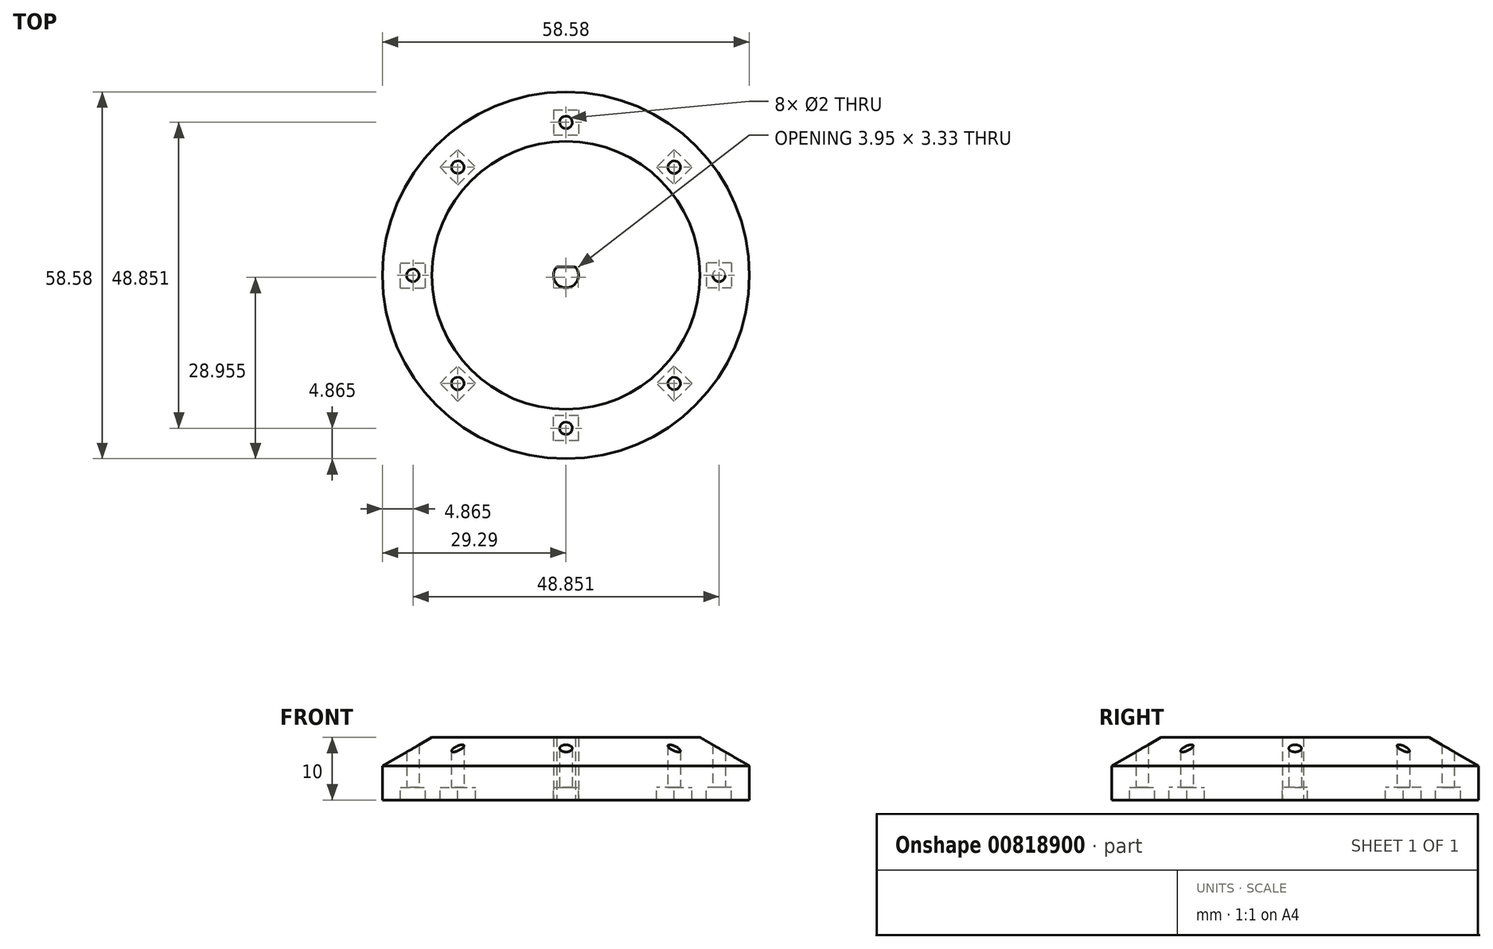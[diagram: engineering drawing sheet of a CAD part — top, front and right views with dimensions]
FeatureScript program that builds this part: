
annotation { "Feature Type Name" : "Feature", "Feature Type Description" : "" }
export const myFeature = defineFeature(function(context is Context, id is Id, definition is map)
    precondition{}
    {
        {
            var Q0;
            Q0=qCreatedBy(makeId("Top.planeOp"),FACE);
            var sketch = newSketch(context, id + "F0", { "sketchPlane" : qUnion([Q0])});
            skCircle(sketch, "E0", {"center": v(0, 0) * mm, "radius": 29.29 * mm});
            skCircle(sketch, "E1", {"center": v(0, 24.43) * mm, "radius": 1 * mm});
            skCircle(sketch, "E2.1.0", {"center": v(-17.27, 17.27) * mm, "radius": 1 * mm});
            skCircle(sketch, "E2.2.0", {"center": v(-24.43, 0) * mm, "radius": 1 * mm});
            skCircle(sketch, "E2.3.0", {"center": v(-17.27, -17.27) * mm, "radius": 1 * mm});
            skCircle(sketch, "E2.4.0", {"center": v(0, -24.43) * mm, "radius": 1 * mm});
            skCircle(sketch, "E2.5.0", {"center": v(17.27, -17.27) * mm, "radius": 1 * mm});
            skCircle(sketch, "E2.6.0", {"center": v(24.43, 0) * mm, "radius": 1 * mm});
            skCircle(sketch, "E2.7.0", {"center": v(17.27, 17.27) * mm, "radius": 1 * mm});
            skArc(sketch, "E3", {"start": v(-1.5, 1.33) * mm, "mid": v(0, -2) * mm, "end": v(1.5, 1.33) * mm});
            skLineSegment(sketch, "E4", {"start": v(-1.5, 1.33) * mm, "end": v(1.5, 1.33) * mm});
            skSolve(sketch);
        }
        {
            var Q0;
            Q0=makeQuery(id+"F0.imprint","IMPRINT",FACE,{"disambiguationData":[TD([[makeQuery(id+"F0.imprint","IMPRINT",EDGE,{"derivedFrom":sQuery(id+"F0.wireOp",EDGE,"E0")}),1.0]])]});
            extrude(context, id + "F1", {"entities" : qUnion([Q0]), "depth" : 10 * mm, "offsetDistance" : 25 * mm});
        }
        {
            var Q0;
            Q0=makeQuery(id+"F1.opExtrude","CAP_EDGE",EDGE,{"disambiguationData":[OSD([sQuery(id+"F0.wireOp",EDGE,"E0")])],"isStart":false});
            chamfer(context, id + "F2", {"entities" : qUnion([Q0]), "chamferType" : ChamferType.TWO_OFFSETS, "width1" : 7.9 * mm, "oppositeDirection" : false, "width2" : 4.56 * mm, "tangentPropagation" : true});
        }
        {
            var Q0;
            Q0=qCreatedBy(makeId("Top.planeOp"),FACE);
            cPlane(context, id + "F3", {"entities" : qUnion([Q0]), "cplaneType" : CPlaneType.OFFSET, "offset" : 2 * mm, "width" : 150 * mm, "height" : 150 * mm});
        }
        {
            var Q0;
            Q0=qCreatedBy(id+"F3.planeOp",FACE);
            var sketch = newSketch(context, id + "F4", { "sketchPlane" : qUnion([Q0])});
            skCircle(sketch, "E5.0", {"center": v(0, -24.43) * mm, "radius": 1 * mm});
            skLineSegment(sketch, "E6.bottom", {"start": v(2, -26.43) * mm, "end": v(-2, -26.43) * mm});
            skLineSegment(sketch, "E6.top", {"start": v(2, -22.43) * mm, "end": v(-2, -22.43) * mm});
            skLineSegment(sketch, "E6.left", {"start": v(2, -26.43) * mm, "end": v(2, -22.43) * mm});
            skLineSegment(sketch, "E6.right", {"start": v(-2, -26.43) * mm, "end": v(-2, -22.43) * mm});
            skLineSegment(sketch, "E7.1.0", {"start": v(20.1, -17.27) * mm, "end": v(17.27, -20.1) * mm});
            skLineSegment(sketch, "E7.1.1", {"start": v(17.27, -20.1) * mm, "end": v(14.44, -17.27) * mm});
            skLineSegment(sketch, "E7.1.2", {"start": v(17.27, -14.44) * mm, "end": v(14.44, -17.27) * mm});
            skLineSegment(sketch, "E7.1.3", {"start": v(20.1, -17.27) * mm, "end": v(17.27, -14.44) * mm});
            skLineSegment(sketch, "E7.2.0", {"start": v(26.43, 2) * mm, "end": v(26.43, -2) * mm});
            skLineSegment(sketch, "E7.2.1", {"start": v(26.43, -2) * mm, "end": v(22.43, -2) * mm});
            skLineSegment(sketch, "E7.2.2", {"start": v(22.43, 2) * mm, "end": v(22.43, -2) * mm});
            skLineSegment(sketch, "E7.2.3", {"start": v(26.43, 2) * mm, "end": v(22.43, 2) * mm});
            skLineSegment(sketch, "E7.3.0", {"start": v(17.27, 20.1) * mm, "end": v(20.1, 17.27) * mm});
            skLineSegment(sketch, "E7.3.1", {"start": v(20.1, 17.27) * mm, "end": v(17.27, 14.44) * mm});
            skLineSegment(sketch, "E7.3.2", {"start": v(14.44, 17.27) * mm, "end": v(17.27, 14.44) * mm});
            skLineSegment(sketch, "E7.3.3", {"start": v(17.27, 20.1) * mm, "end": v(14.44, 17.27) * mm});
            skLineSegment(sketch, "E7.4.0", {"start": v(-2, 26.43) * mm, "end": v(2, 26.43) * mm});
            skLineSegment(sketch, "E7.4.1", {"start": v(2, 26.43) * mm, "end": v(2, 22.43) * mm});
            skLineSegment(sketch, "E7.4.2", {"start": v(-2, 22.43) * mm, "end": v(2, 22.43) * mm});
            skLineSegment(sketch, "E7.4.3", {"start": v(-2, 26.43) * mm, "end": v(-2, 22.43) * mm});
            skLineSegment(sketch, "E7.5.0", {"start": v(-20.1, 17.27) * mm, "end": v(-17.27, 20.1) * mm});
            skLineSegment(sketch, "E7.5.1", {"start": v(-17.27, 20.1) * mm, "end": v(-14.44, 17.27) * mm});
            skLineSegment(sketch, "E7.5.2", {"start": v(-17.27, 14.44) * mm, "end": v(-14.44, 17.27) * mm});
            skLineSegment(sketch, "E7.5.3", {"start": v(-20.1, 17.27) * mm, "end": v(-17.27, 14.44) * mm});
            skLineSegment(sketch, "E7.6.0", {"start": v(-26.43, -2) * mm, "end": v(-26.43, 2) * mm});
            skLineSegment(sketch, "E7.6.1", {"start": v(-26.43, 2) * mm, "end": v(-22.43, 2) * mm});
            skLineSegment(sketch, "E7.6.2", {"start": v(-22.43, -2) * mm, "end": v(-22.43, 2) * mm});
            skLineSegment(sketch, "E7.6.3", {"start": v(-26.43, -2) * mm, "end": v(-22.43, -2) * mm});
            skLineSegment(sketch, "E7.7.0", {"start": v(-17.27, -20.1) * mm, "end": v(-20.1, -17.27) * mm});
            skLineSegment(sketch, "E7.7.1", {"start": v(-20.1, -17.27) * mm, "end": v(-17.27, -14.44) * mm});
            skLineSegment(sketch, "E7.7.2", {"start": v(-14.44, -17.27) * mm, "end": v(-17.27, -14.44) * mm});
            skLineSegment(sketch, "E7.7.3", {"start": v(-17.27, -20.1) * mm, "end": v(-14.44, -17.27) * mm});
            skPoint(sketch, "E7.center", {"position": v(0, 0) * mm});
            skSolve(sketch);
        }
        {
            var Q0;
            Q0=makeQuery(id+"F4.imprint","IMPRINT",FACE,{"disambiguationData":[TD([[makeQuery(id+"F4.imprint","IMPRINT",EDGE,{"derivedFrom":sQuery(id+"F4.wireOp",EDGE,"E5.0")}),1.0]])]});
            var Q1;
            Q1=makeQuery(id+"F4.imprint","IMPRINT",FACE,{"disambiguationData":[TD([[makeQuery(id+"F4.imprint","IMPRINT",EDGE,{"derivedFrom":sQuery(id+"F4.wireOp",EDGE,"E5.0")}),-1.0]])]});
            var Q2;
            Q2=makeQuery(id+"F4.imprint","IMPRINT",FACE,{"disambiguationData":[TD([[makeQuery(id+"F4.imprint","IMPRINT",EDGE,{"derivedFrom":sQuery(id+"F4.wireOp",EDGE,"E7.7.0")}),-1.0]])]});
            var Q3;
            Q3=makeQuery(id+"F4.imprint","IMPRINT",FACE,{"disambiguationData":[TD([[makeQuery(id+"F4.imprint","IMPRINT",EDGE,{"derivedFrom":sQuery(id+"F4.wireOp",EDGE,"E7.1.0")}),-1.0]])]});
            var Q4;
            Q4=makeQuery(id+"F4.imprint","IMPRINT",FACE,{"disambiguationData":[TD([[makeQuery(id+"F4.imprint","IMPRINT",EDGE,{"derivedFrom":sQuery(id+"F4.wireOp",EDGE,"E7.6.0")}),-1.0]])]});
            var Q5;
            Q5=makeQuery(id+"F4.imprint","IMPRINT",FACE,{"disambiguationData":[TD([[makeQuery(id+"F4.imprint","IMPRINT",EDGE,{"derivedFrom":sQuery(id+"F4.wireOp",EDGE,"E7.2.0")}),-1.0]])]});
            var Q6;
            Q6=makeQuery(id+"F4.imprint","IMPRINT",FACE,{"disambiguationData":[TD([[makeQuery(id+"F4.imprint","IMPRINT",EDGE,{"derivedFrom":sQuery(id+"F4.wireOp",EDGE,"E7.5.0")}),-1.0]])]});
            var Q7;
            Q7=makeQuery(id+"F4.imprint","IMPRINT",FACE,{"disambiguationData":[TD([[makeQuery(id+"F4.imprint","IMPRINT",EDGE,{"derivedFrom":sQuery(id+"F4.wireOp",EDGE,"E7.3.0")}),-1.0]])]});
            var Q8;
            Q8=makeQuery(id+"F4.imprint","IMPRINT",FACE,{"disambiguationData":[TD([[makeQuery(id+"F4.imprint","IMPRINT",EDGE,{"derivedFrom":sQuery(id+"F4.wireOp",EDGE,"E7.4.0")}),-1.0]])]});
            extrude(context, id + "F5", {"entities" : qUnion([Q0, Q1, Q2, Q3, Q4, Q5, Q6, Q7, Q8]), "operationType" : NewBodyOperationType.REMOVE, "oppositeDirection" : true, "depth" : 2 * mm, "offsetDistance" : 25 * mm});
        }
    });
